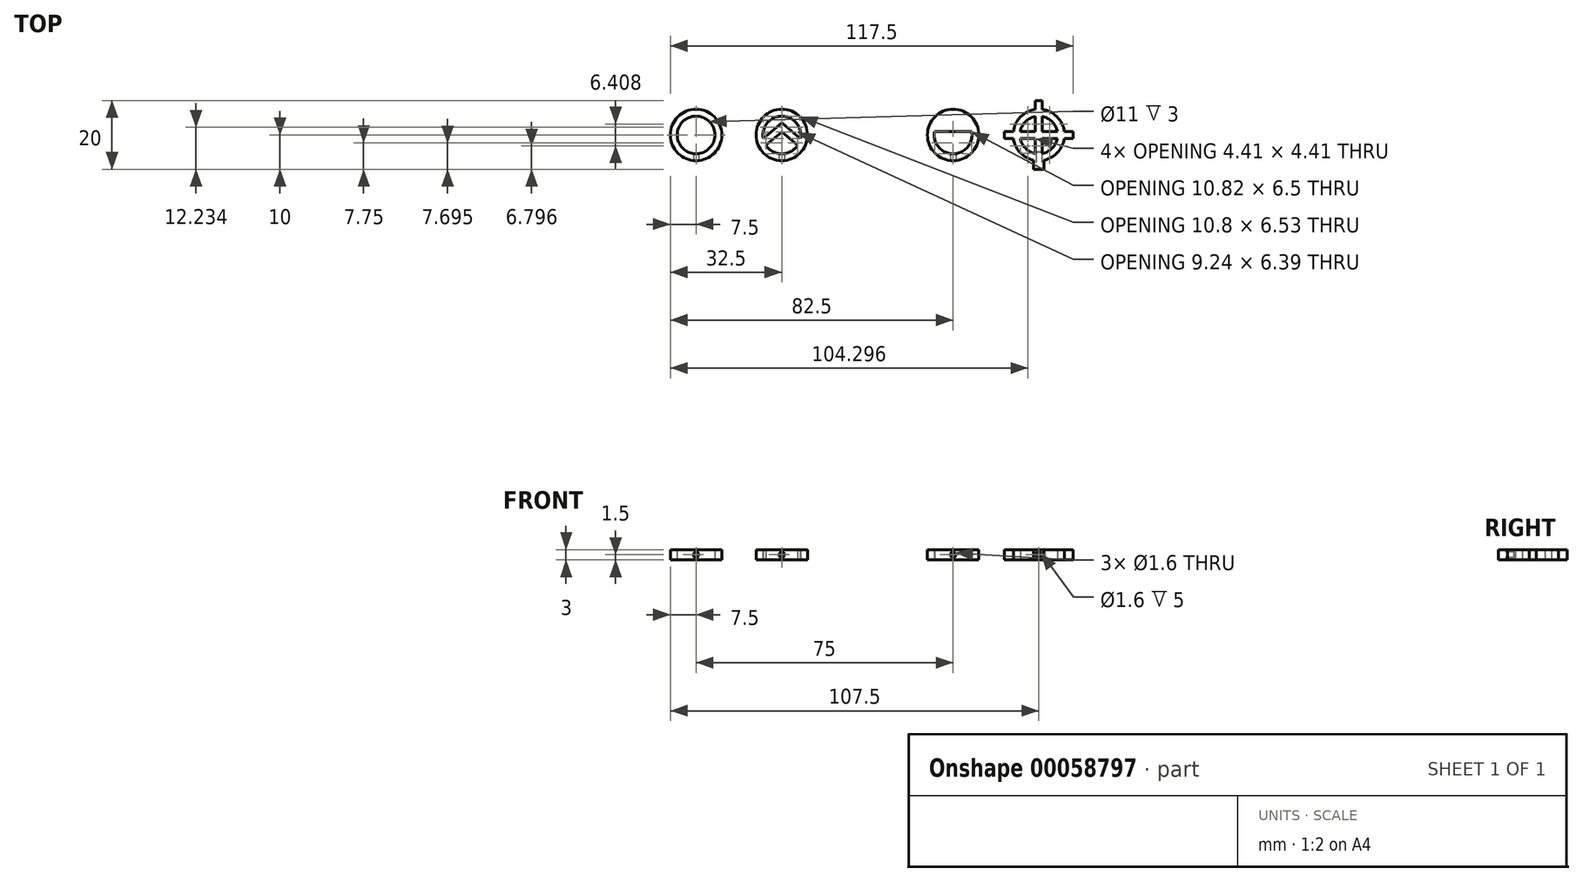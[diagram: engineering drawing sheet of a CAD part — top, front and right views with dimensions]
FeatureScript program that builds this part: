
annotation { "Feature Type Name" : "Feature", "Feature Type Description" : "" }
export const myFeature = defineFeature(function(context is Context, id is Id, definition is map)
    precondition{}
    {
        {
            var Q0;
            Q0=qCreatedBy(makeId("Top.planeOp"),FACE);
            var sketch = newSketch(context, id + "F0", { "sketchPlane" : qUnion([Q0])});
            skCircle(sketch, "E0", {"center": v(50, 0) * mm, "radius": 7.5 * mm});
            skCircle(sketch, "E1", {"center": v(50, 0) * mm, "radius": 5.5 * mm});
            skCircle(sketch, "E2", {"center": v(25, 0) * mm, "radius": 7.5 * mm});
            skCircle(sketch, "E3", {"center": v(25, 0) * mm, "radius": 5.5 * mm});
            skCircle(sketch, "E4", {"center": v(-25, 0) * mm, "radius": 7.5 * mm});
            skCircle(sketch, "E5", {"center": v(-25, 0) * mm, "radius": 5.5 * mm});
            skCircle(sketch, "E6", {"center": v(-50, 0) * mm, "radius": 7.5 * mm});
            skCircle(sketch, "E7", {"center": v(-50, 0) * mm, "radius": 5.5 * mm});
            skLineSegment(sketch, "E8.bottom", {"start": v(49, 10) * mm, "end": v(51, 10) * mm});
            skLineSegment(sketch, "E8.top", {"start": v(49, -10) * mm, "end": v(51, -10) * mm});
            skLineSegment(sketch, "E8.left", {"start": v(49, 10) * mm, "end": v(49, -10) * mm});
            skLineSegment(sketch, "E8.right", {"start": v(51, 10) * mm, "end": v(51, -10) * mm});
            skLineSegment(sketch, "E9.bottom", {"start": v(60, -1) * mm, "end": v(40, -1) * mm});
            skLineSegment(sketch, "E9.top", {"start": v(60, 1) * mm, "end": v(40, 1) * mm});
            skLineSegment(sketch, "E9.left", {"start": v(60, -1) * mm, "end": v(60, 1) * mm});
            skLineSegment(sketch, "E9.right", {"start": v(40, -1) * mm, "end": v(40, 1) * mm});
            skLineSegment(sketch, "E10.bottom", {"start": v(17.57, 1) * mm, "end": v(32.43, 1) * mm});
            skLineSegment(sketch, "E10.top", {"start": v(17.57, -1) * mm, "end": v(32.43, -1) * mm});
            skLineSegment(sketch, "E10.left", {"start": v(17.57, 1) * mm, "end": v(17.57, -1) * mm});
            skLineSegment(sketch, "E10.right", {"start": v(32.43, 1) * mm, "end": v(32.43, -1) * mm});
            skLineSegment(sketch, "E11.bottom", {"start": v(51.5, -10) * mm, "end": v(48.5, -10) * mm});
            skLineSegment(sketch, "E11.top", {"start": v(51.5, -7.35) * mm, "end": v(48.5, -7.35) * mm});
            skLineSegment(sketch, "E11.left", {"start": v(51.5, -10) * mm, "end": v(51.5, -7.35) * mm});
            skLineSegment(sketch, "E11.right", {"start": v(48.5, -10) * mm, "end": v(48.5, -7.35) * mm});
            skPoint(sketch, "E11.middle", {"position": v(50, -8.67) * mm});
            skLineSegment(sketch, "E12", {"start": v(-30.4, -1.03) * mm, "end": v(-25, 3.5) * mm});
            skLineSegment(sketch, "E13", {"start": v(-25, 3.5) * mm, "end": v(-19.6, -1.03) * mm});
            skLineSegment(sketch, "E14", {"start": v(-29.62, -2.99) * mm, "end": v(-25, 0.89) * mm});
            skLineSegment(sketch, "E15", {"start": v(-25, 0.89) * mm, "end": v(-20.38, -2.99) * mm});
            skSolve(sketch);
        }
        {
            var Q0;
            Q0 = qSketchRegion(id + "F0", true);
            var Q1;
            {var subQ0=sQuery(id+"F0.wireOp",EDGE,"E10.bottom");var subQ1=sQuery(id+"F0.wireOp",EDGE,"E3");var subQ2=makeQuery(id+"F0.imprint","INTERSECT",VERTEX,{"disambiguationData":[OD(0.0)],"derivedFrom":[subQ1,subQ0]});Q1=makeQuery(id+"F0.imprint","IMPRINT",FACE,{"disambiguationData":[TD([[makeQuery(id+"F0.imprint","IMPRINT",EDGE,{"disambiguationData":[TD([[subQ2,-1.0]])],"derivedFrom":subQ1}),1.0]])]});}
            var Q2;
            {var subQ0=sQuery(id+"F0.wireOp",EDGE,"E9.top");var subQ1=sQuery(id+"F0.wireOp",EDGE,"E8.left");var subQ2=makeQuery(id+"F0.imprint","INTERSECT",VERTEX,{"derivedFrom":[subQ1,subQ0]});Q2=makeQuery(id+"F0.imprint","IMPRINT",FACE,{"disambiguationData":[TD([[makeQuery(id+"F0.imprint","IMPRINT",EDGE,{"disambiguationData":[TD([[subQ2,-1.0]])],"derivedFrom":subQ1}),1.0]])]});}
            var Q3;
            {var subQ0=sQuery(id+"F0.wireOp",EDGE,"E9.top");var subQ1=sQuery(id+"F0.wireOp",EDGE,"E1");var subQ2=makeQuery(id+"F0.imprint","INTERSECT",VERTEX,{"disambiguationData":[OD(0.0)],"derivedFrom":[subQ1,subQ0]});Q3=makeQuery(id+"F0.imprint","IMPRINT",FACE,{"disambiguationData":[TD([[makeQuery(id+"F0.imprint","IMPRINT",EDGE,{"disambiguationData":[TD([[subQ2,1.0]])],"derivedFrom":subQ1}),1.0]])]});}
            var Q4;
            {var subQ0=sQuery(id+"F0.wireOp",EDGE,"E8.right");var subQ1=sQuery(id+"F0.wireOp",EDGE,"E1");var subQ2=makeQuery(id+"F0.imprint","INTERSECT",VERTEX,{"disambiguationData":[OD(0.0)],"derivedFrom":[subQ1,subQ0]});Q4=makeQuery(id+"F0.imprint","IMPRINT",FACE,{"disambiguationData":[TD([[makeQuery(id+"F0.imprint","IMPRINT",EDGE,{"disambiguationData":[TD([[subQ2,-1.0]])],"derivedFrom":subQ1}),1.0]])]});}
            var Q5;
            {var subQ0=sQuery(id+"F0.wireOp",EDGE,"E9.top");var subQ1=sQuery(id+"F0.wireOp",EDGE,"E1");var subQ2=makeQuery(id+"F0.imprint","INTERSECT",VERTEX,{"disambiguationData":[OD(1.0)],"derivedFrom":[subQ1,subQ0]});Q5=makeQuery(id+"F0.imprint","IMPRINT",FACE,{"disambiguationData":[TD([[makeQuery(id+"F0.imprint","IMPRINT",EDGE,{"disambiguationData":[TD([[subQ2,-1.0]])],"derivedFrom":subQ1}),1.0]])]});}
            var Q6;
            {var subQ0=sQuery(id+"F0.wireOp",EDGE,"E8.left");var subQ1=sQuery(id+"F0.wireOp",EDGE,"E1");var subQ2=makeQuery(id+"F0.imprint","INTERSECT",VERTEX,{"disambiguationData":[OD(1.0)],"derivedFrom":[subQ1,subQ0]});Q6=makeQuery(id+"F0.imprint","IMPRINT",FACE,{"disambiguationData":[TD([[makeQuery(id+"F0.imprint","IMPRINT",EDGE,{"disambiguationData":[TD([[subQ2,-1.0]])],"derivedFrom":subQ1}),1.0]])]});}
            var Q7;
            {var subQ0=sQuery(id+"F0.wireOp",EDGE,"E8.left");var subQ1=sQuery(id+"F0.wireOp",EDGE,"E1");var subQ2=makeQuery(id+"F0.imprint","INTERSECT",VERTEX,{"disambiguationData":[OD(1.0)],"derivedFrom":[subQ1,subQ0]});Q7=makeQuery(id+"F0.imprint","IMPRINT",FACE,{"disambiguationData":[TD([[makeQuery(id+"F0.imprint","IMPRINT",EDGE,{"disambiguationData":[TD([[subQ2,-1.0]])],"derivedFrom":subQ1}),-1.0]])]});}
            var Q8;
            {var subQ0=sQuery(id+"F0.wireOp",EDGE,"E8.left");var subQ1=sQuery(id+"F0.wireOp",EDGE,"E0");var subQ2=makeQuery(id+"F0.imprint","INTERSECT",VERTEX,{"disambiguationData":[OD(1.0)],"derivedFrom":[subQ1,subQ0]});Q8=makeQuery(id+"F0.imprint","IMPRINT",FACE,{"disambiguationData":[TD([[makeQuery(id+"F0.imprint","IMPRINT",EDGE,{"disambiguationData":[TD([[subQ2,-1.0]])],"derivedFrom":subQ1}),1.0]])]});}
            var Q9;
            {var subQ4=sQuery(id+"F0.wireOp",EDGE,"E12");Q9=makeQuery(id+"F0.imprint","IMPRINT",FACE,{"disambiguationData":[TD([[makeQuery(id+"F0.imprint","IMPRINT",EDGE,{"derivedFrom":subQ4}),-1.0]])]});}
            extrude(context, id + "F1", {"entities" : qUnion([Q0, Q1, Q2, Q3, Q4, Q5, Q6, Q7, Q8, Q9]), "depth" : 3 * mm, "symmetric" : true});
        }
        {
            var Q0;
            Q0=makeQuery(id+"F1.opExtrude","SWEPT_FACE",FACE,{"disambiguationData":[OSD([sQuery(id+"F0.wireOp",EDGE,"E11.bottom")])]});
            var sketch = newSketch(context, id + "F2", { "sketchPlane" : qUnion([Q0])});
            skCircle(sketch, "E16", {"center": v(50, 0) * mm, "radius": 0.8 * mm});
            skPoint(sketch, "E16.centerSnap0", {"position": v(50, -1.5) * mm});
            skCircle(sketch, "E17", {"center": v(25, 0) * mm, "radius": 0.8 * mm});
            skCircle(sketch, "E18", {"center": v(-25, 0) * mm, "radius": 0.8 * mm});
            skCircle(sketch, "E19", {"center": v(-50, 0) * mm, "radius": 0.8 * mm});
            skSolve(sketch);
        }
        {
            var Q0;
            Q0=makeQuery(id+"F2.imprint","IMPRINT",FACE,{"disambiguationData":[TD([[makeQuery(id+"F2.imprint","IMPRINT",EDGE,{"derivedFrom":sQuery(id+"F2.wireOp",EDGE,"E16")}),1.0]])]});
            var Q1;
            Q1=makeQuery(id+"F2.imprint","IMPRINT",FACE,{"disambiguationData":[TD([[makeQuery(id+"F2.imprint","IMPRINT",EDGE,{"derivedFrom":sQuery(id+"F2.wireOp",EDGE,"E17")}),1.0]])]});
            var Q2;
            Q2=makeQuery(id+"F2.imprint","IMPRINT",FACE,{"disambiguationData":[TD([[makeQuery(id+"F2.imprint","IMPRINT",EDGE,{"derivedFrom":sQuery(id+"F2.wireOp",EDGE,"E18")}),1.0]])]});
            var Q3;
            Q3=makeQuery(id+"F2.imprint","IMPRINT",FACE,{"disambiguationData":[TD([[makeQuery(id+"F2.imprint","IMPRINT",EDGE,{"derivedFrom":sQuery(id+"F2.wireOp",EDGE,"E19")}),1.0]])]});
            extrude(context, id + "F3", {"entities" : qUnion([Q0, Q1, Q2, Q3]), "operationType" : NewBodyOperationType.REMOVE, "oppositeDirection" : true, "depth" : 5 * mm});
        }
    });
